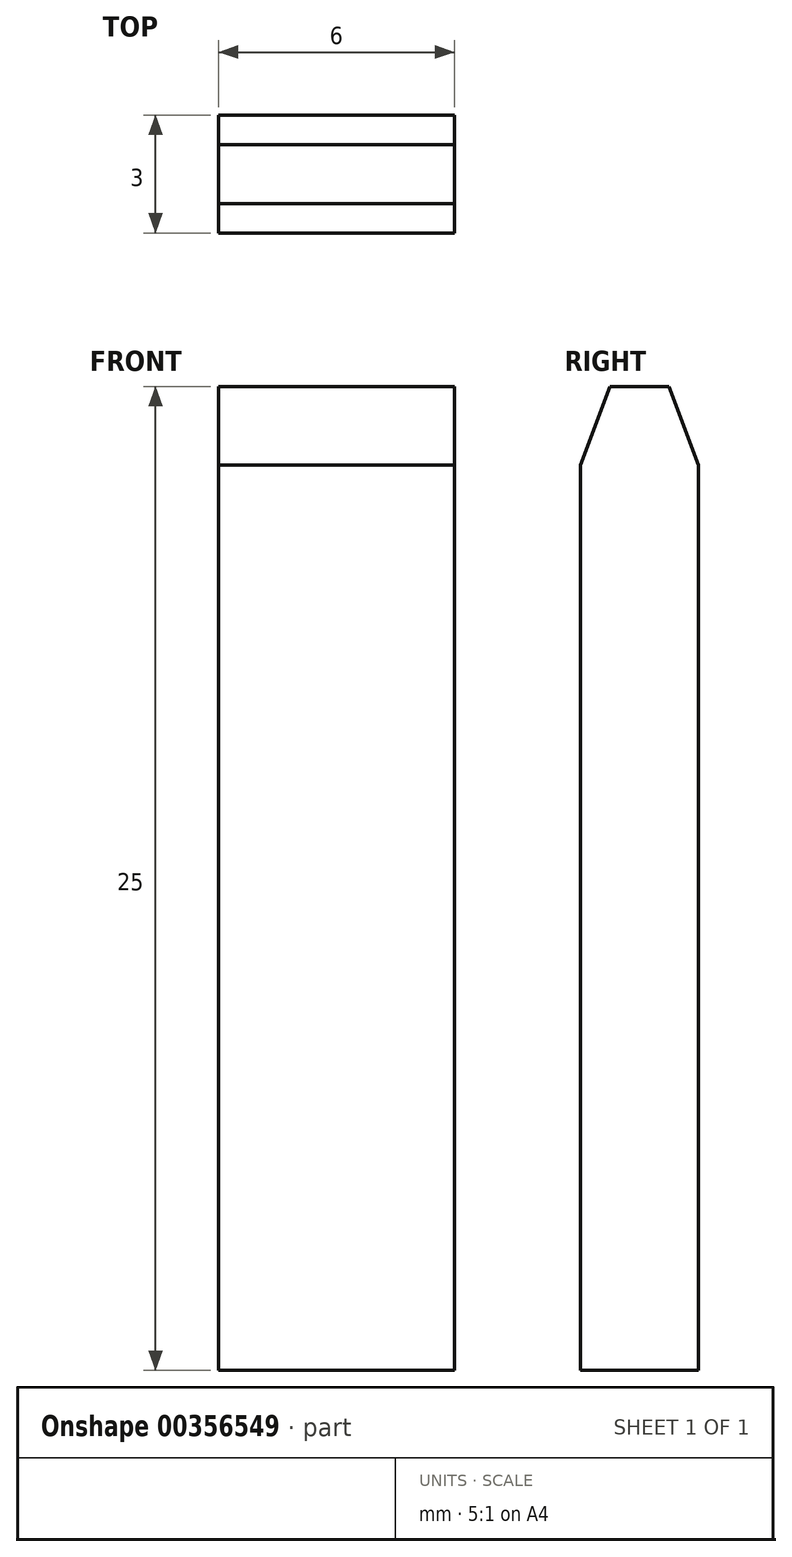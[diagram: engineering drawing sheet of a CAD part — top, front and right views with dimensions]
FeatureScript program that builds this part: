
annotation { "Feature Type Name" : "Feature", "Feature Type Description" : "" }
export const myFeature = defineFeature(function(context is Context, id is Id, definition is map)
    precondition{}
    {
        {
            var Q0;
            Q0=qCreatedBy(makeId("Top.planeOp"),FACE);
            var sketch = newSketch(context, id + "F0", { "sketchPlane" : qUnion([Q0])});
            skLineSegment(sketch, "E0.bottom", {"start": v(4.89, -4.56) * mm, "end": v(10.89, -4.56) * mm});
            skLineSegment(sketch, "E0.top", {"start": v(4.89, -7.56) * mm, "end": v(10.89, -7.56) * mm});
            skLineSegment(sketch, "E0.left", {"start": v(4.89, -4.56) * mm, "end": v(4.89, -7.56) * mm});
            skLineSegment(sketch, "E0.right", {"start": v(10.89, -4.56) * mm, "end": v(10.89, -7.56) * mm});
            skSolve(sketch);
        }
        {
            var Q0;
            Q0=makeQuery(id+"F0.imprint","IMPRINT",FACE,{"disambiguationData":[TD([[makeQuery(id+"F0.imprint","IMPRINT",EDGE,{"derivedFrom":sQuery(id+"F0.wireOp",EDGE,"E0.bottom")}),-1.0]])]});
            extrude(context, id + "F1", {"entities" : qUnion([Q0]), "depth" : 25 * mm});
        }
        {
            var Q0;
            Q0=makeQuery(id+"F1.opExtrude","CAP_EDGE",EDGE,{"disambiguationData":[OSD([sQuery(id+"F0.wireOp",EDGE,"E0.top")])],"isStart":false});
            var Q1;
            Q1=makeQuery(id+"F1.opExtrude","CAP_EDGE",EDGE,{"disambiguationData":[OSD([sQuery(id+"F0.wireOp",EDGE,"E0.bottom")])],"isStart":false});
            chamfer(context, id + "F2", {"entities" : qUnion([Q0, Q1]), "chamferType" : ChamferType.TWO_OFFSETS, "width1" : 0.75 * mm, "oppositeDirection" : false, "width2" : 2 * mm, "tangentPropagation" : true});
        }
    });
